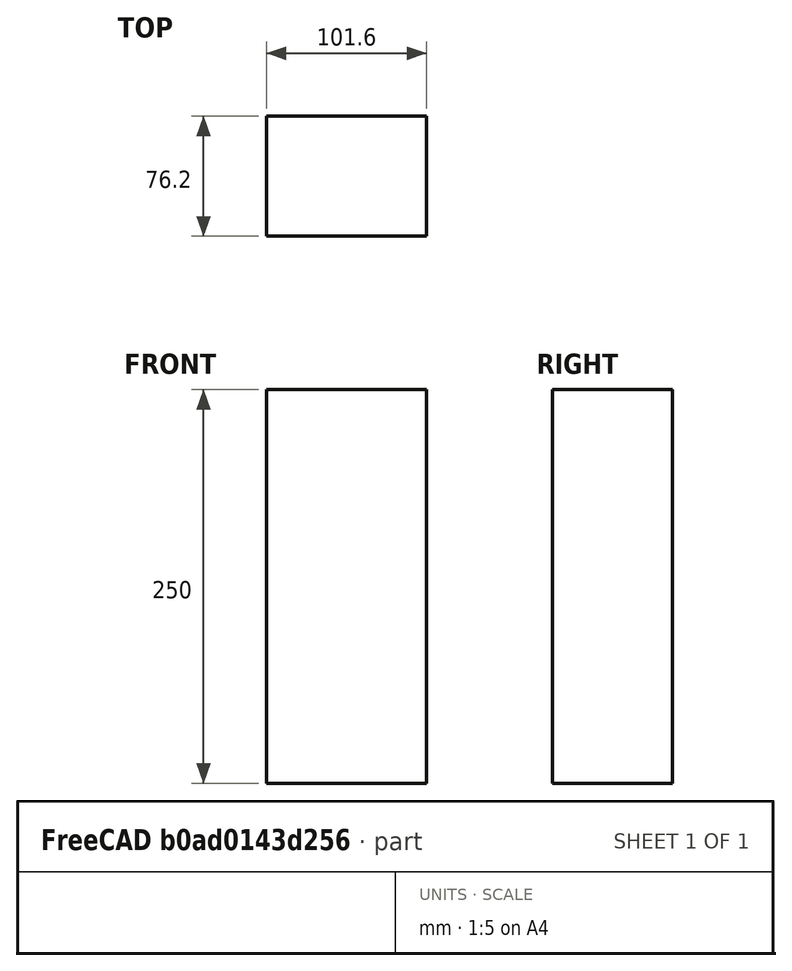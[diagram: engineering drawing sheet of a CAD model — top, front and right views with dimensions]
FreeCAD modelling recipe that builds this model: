
FCSTD DOCUMENT  (FreeCAD 1.0R39109 (Git))
Label: Shamrock
License: All rights reserved
LicenseURL: https://en.wikipedia.org/wiki/All_rights_reserved
objects: PartDesign::CoordinateSystem×2, App::DocumentObjectGroup×2, Sketcher::SketchObject×1, PartDesign::Pad×1, PartDesign::Body×1, App::FeaturePython×1, App::Part×1
note: 8 computed .brp shape members not serialized (recipe doc carries the construction recipe); baked Part::Feature solids carry a one-line shape summary decoded from their .brp

FEATURE [Sketcher::SketchObject] Sketch
  ArcFitTolerance = 1e-06
  AttachmentSupport = -> [XY_Plane]
  FullyConstrained = true
  MakeInternals = false
  MapMode = 5
  sketch-geometry (4):
    g0: LineSegment StartX=-50.8 StartY=38.1 StartZ=0 EndX=-50.8 EndY=-38.1 EndZ=0
    g1: LineSegment StartX=-50.8 StartY=-38.1 StartZ=0 EndX=50.8 EndY=-38.1 EndZ=0
    g2: LineSegment StartX=50.8 StartY=-38.1 StartZ=0 EndX=50.8 EndY=38.1 EndZ=0
    g3: LineSegment StartX=50.8 StartY=38.1 StartZ=0 EndX=-50.8 EndY=38.1 EndZ=0
  constraints (12):
    c: Coincident(g0,g1)
    c: Coincident(g1,g2)
    c: Coincident(g2,g3)
    c: Coincident(g3,g0)
    c: Vertical(g0)
    c: Vertical(g2)
    c: Horizontal(g1)
    c: Horizontal(g3)
    c: DistanceX(g3,g3) = 101.6
    c: DistanceY(g0,g0) = 76.2
    c: DistanceX(g0,g-1) = 50.8
    c: DistanceY(g-1,g2) = 38.1
FEATURE [PartDesign::Pad] Pad
  Direction = (0,0,1)
  Length = 250
  Length2 = 10
  Profile = -> Sketch
  ReferenceAxis = -> Sketch [N_Axis]
  Suppressed = false
  Type = 0
FEATURE [PartDesign::Body] Body
  AllowCompound = false
  Group = -> [Sketch,Pad]
  Origin = -> Origin
  Tip = -> Pad
FEATURE [PartDesign::CoordinateSystem] LCS_Origin
  AttacherType = Attacher::AttachEngine3D
  AttachmentSupport = -> [X_Axis001]
  MapMode = 2
FEATURE [App::DocumentObjectGroup] Constraints
FEATURE [App::FeaturePython] Variables  # WARN: FeaturePython — macro-defined, semantics opaque (R4)
  Type = App::PropertyContainer
FEATURE [App::DocumentObjectGroup] Configurations
FEATURE [PartDesign::CoordinateSystem] LCS_1
  AttacherType = Attacher::AttachEngine3D
  Placement = pos=(50.8,0,0) rot=(0,0,1;1.5708rad)
FEATURE [App::Part] Assembly
  AssemblyType = Part::Link
  Group = -> [LCS_Origin,Constraints,Variables,Configurations,Body,LCS_1]
  Origin = -> Origin001
  Type = Assembly
